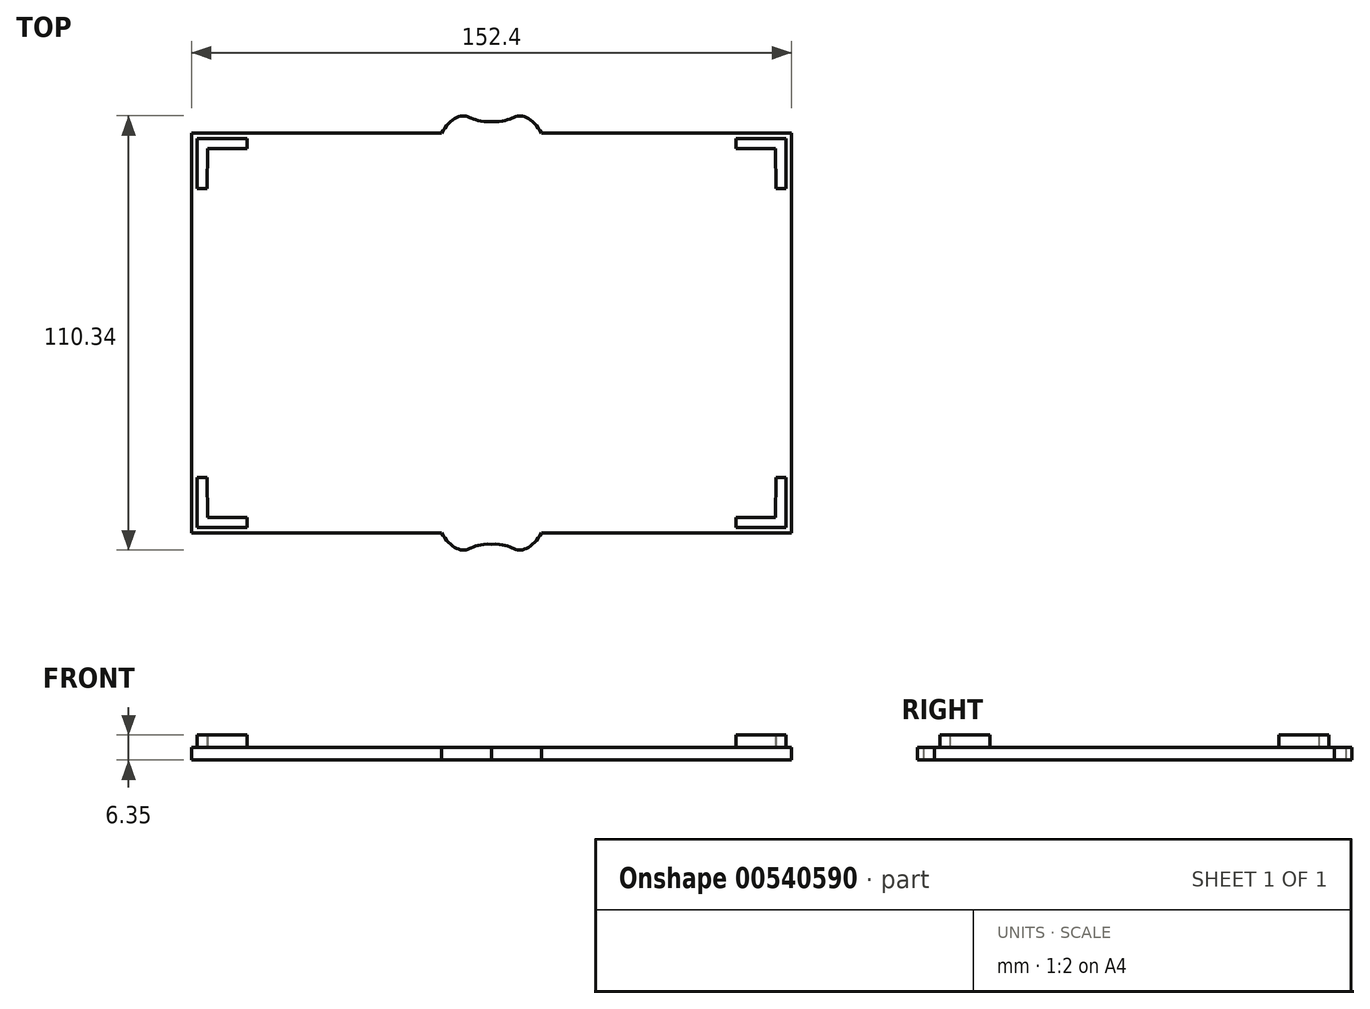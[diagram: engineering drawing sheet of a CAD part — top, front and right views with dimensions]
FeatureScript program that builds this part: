
annotation { "Feature Type Name" : "Feature", "Feature Type Description" : "" }
export const myFeature = defineFeature(function(context is Context, id is Id, definition is map)
    precondition{}
    {
        {
            var Q0;
            Q0=qCreatedBy(makeId("Top.planeOp"),FACE);
            var sketch = newSketch(context, id + "F0", { "sketchPlane" : qUnion([Q0])});
            skLineSegment(sketch, "E0.bottom", {"start": v(-76.2, 50.9) * mm, "end": v(76.2, 50.9) * mm});
            skLineSegment(sketch, "E0.top", {"start": v(-76.2, -50.7) * mm, "end": v(76.2, -50.7) * mm});
            skLineSegment(sketch, "E0.left", {"start": v(-76.2, 50.9) * mm, "end": v(-76.2, -50.7) * mm});
            skLineSegment(sketch, "E0.right", {"start": v(76.2, 50.9) * mm, "end": v(76.2, -50.7) * mm});
            skPoint(sketch, "E1", {"position": v(0.17, 0.1) * mm});
            skLineSegment(sketch, "E2.bottom", {"start": v(-74.8, 49.5) * mm, "end": v(-62.1, 49.5) * mm});
            skLineSegment(sketch, "E2.left", {"start": v(-74.8, 49.5) * mm, "end": v(-74.8, 36.8) * mm});
            skLineSegment(sketch, "E3", {"start": v(-38.1, 62.37) * mm, "end": v(-38.1, -57.09) * mm, "construction": true});
            skLineSegment(sketch, "E4", {"start": v(0, 53.8) * mm, "end": v(0, -66.57) * mm, "construction": true});
            skLineSegment(sketch, "E5", {"start": v(38.1, 55.38) * mm, "end": v(38.1, -59.8) * mm, "construction": true});
            skLineSegment(sketch, "E6", {"start": v(85.14, 0.1) * mm, "end": v(-105.52, 0.1) * mm, "construction": true});
            skPoint(sketch, "E7", {"position": v(-72.1, 46.95) * mm});
            skLineSegment(sketch, "E8", {"start": v(-62.1, 49.5) * mm, "end": v(-62.1, 46.95) * mm});
            skLineSegment(sketch, "E9", {"start": v(-72.26, 36.8) * mm, "end": v(-74.8, 36.8) * mm});
            skLineSegment(sketch, "E10", {"start": v(-72.26, 36.8) * mm, "end": v(-72.1, 46.95) * mm});
            skLineSegment(sketch, "E11", {"start": v(-72.1, 46.95) * mm, "end": v(-62.1, 46.95) * mm});
            skLineSegment(sketch, "E12.MirrorCS", {"start": v(72.1, 46.95) * mm, "end": v(62.1, 46.95) * mm});
            skLineSegment(sketch, "E13.MirrorCS", {"start": v(62.1, 49.5) * mm, "end": v(62.1, 46.95) * mm});
            skLineSegment(sketch, "E14.MirrorCS", {"start": v(74.8, 49.5) * mm, "end": v(62.1, 49.5) * mm});
            skLineSegment(sketch, "E15.MirrorCS", {"start": v(74.8, 49.5) * mm, "end": v(74.8, 36.8) * mm});
            skLineSegment(sketch, "E16.MirrorCS", {"start": v(72.26, 36.8) * mm, "end": v(72.1, 46.95) * mm});
            skLineSegment(sketch, "E17.MirrorCS", {"start": v(72.26, 36.8) * mm, "end": v(74.8, 36.8) * mm});
            skLineSegment(sketch, "E18.MirrorCS", {"start": v(-74.8, -49.31) * mm, "end": v(-62.1, -49.31) * mm});
            skLineSegment(sketch, "E19.MirrorCS", {"start": v(-62.1, -49.31) * mm, "end": v(-62.1, -46.77) * mm});
            skLineSegment(sketch, "E20.MirrorCS", {"start": v(-72.1, -46.77) * mm, "end": v(-62.1, -46.77) * mm});
            skLineSegment(sketch, "E21.MirrorCS", {"start": v(-74.8, -49.31) * mm, "end": v(-74.8, -36.61) * mm});
            skLineSegment(sketch, "E22.MirrorCS", {"start": v(-72.26, -36.61) * mm, "end": v(-72.1, -46.77) * mm});
            skLineSegment(sketch, "E23.MirrorCS", {"start": v(-72.26, -36.61) * mm, "end": v(-74.8, -36.61) * mm});
            skLineSegment(sketch, "E24.MirrorCS", {"start": v(74.8, -49.31) * mm, "end": v(62.1, -49.31) * mm});
            skLineSegment(sketch, "E25.MirrorCS", {"start": v(62.1, -49.31) * mm, "end": v(62.1, -46.77) * mm});
            skLineSegment(sketch, "E26.MirrorCS", {"start": v(72.1, -46.77) * mm, "end": v(62.1, -46.77) * mm});
            skLineSegment(sketch, "E27.MirrorCS", {"start": v(74.8, -49.31) * mm, "end": v(74.8, -36.61) * mm});
            skLineSegment(sketch, "E28.MirrorCS", {"start": v(72.26, -36.61) * mm, "end": v(72.1, -46.77) * mm});
            skLineSegment(sketch, "E29.MirrorCS", {"start": v(72.26, -36.61) * mm, "end": v(74.8, -36.61) * mm});
            skLineSegment(sketch, "E30", {"start": v(-12.7, 55.26) * mm, "end": v(-12.7, 40.9) * mm, "construction": true});
            skLineSegment(sketch, "E31", {"start": v(12.7, 54.7) * mm, "end": v(12.7, 43.66) * mm, "construction": true});
            skPoint(sketch, "E32", {"position": v(-12.7, 50.9) * mm});
            skFitSpline(sketch, "E33", {"points": [v(-12.7, 50.9) * mm, v(-7.3, 55.26) * mm, v(0, 53.8) * mm], "startDerivative": vector(9.09, 15.87) * mm, "endDerivative": vector(24.9, 1.73) * mm});
            skFitSpline(sketch, "E34.MirrorCS", {"points": [v(12.7, 50.9) * mm, v(7.3, 55.26) * mm, v(0, 53.8) * mm], "startDerivative": vector(-9.09, 15.87) * mm, "endDerivative": vector(-24.9, 1.73) * mm});
            skFitSpline(sketch, "E35.MirrorCS", {"points": [v(-12.7, -50.7) * mm, v(-7.3, -55.08) * mm, v(0, -53.61) * mm], "startDerivative": vector(9.09, -15.87) * mm, "endDerivative": vector(24.9, -1.73) * mm});
            skFitSpline(sketch, "E36.MirrorCS", {"points": [v(12.7, -50.7) * mm, v(7.3, -55.08) * mm, v(0, -53.61) * mm], "startDerivative": vector(-9.09, -15.87) * mm, "endDerivative": vector(-24.9, -1.73) * mm});
            skSolve(sketch);
        }
        {
            var Q0;
            {var subQ0=sQuery(id+"F0.wireOp",EDGE,"E0.left");Q0=makeQuery(id+"F0.imprint","IMPRINT",FACE,{"disambiguationData":[TD([[makeQuery(id+"F0.imprint","IMPRINT",EDGE,{"derivedFrom":subQ0}),1.0]])]});}
            var Q1;
            {var subQ0=sQuery(id+"F0.wireOp",EDGE,"E35.MirrorCS");Q1=makeQuery(id+"F0.imprint","IMPRINT",FACE,{"disambiguationData":[TD([[makeQuery(id+"F0.imprint","IMPRINT",EDGE,{"derivedFrom":subQ0}),1.0]])]});}
            var Q2;
            {var subQ0=sQuery(id+"F0.wireOp",EDGE,"E33");Q2=makeQuery(id+"F0.imprint","IMPRINT",FACE,{"disambiguationData":[TD([[makeQuery(id+"F0.imprint","IMPRINT",EDGE,{"derivedFrom":subQ0}),-1.0]])]});}
            extrude(context, id + "F1", {"entities" : qUnion([Q0, Q1, Q2]), "depth" : 3.17 * mm, "offsetDistance" : 25.4 * mm});
        }
        {
            var Q0;
            Q0=makeQuery(id+"F0.imprint","IMPRINT",FACE,{"disambiguationData":[TD([[makeQuery(id+"F0.imprint","IMPRINT",EDGE,{"derivedFrom":sQuery(id+"F0.wireOp",EDGE,"E18.MirrorCS")}),1.0]])]});
            var Q1;
            Q1=makeQuery(id+"F0.imprint","IMPRINT",FACE,{"disambiguationData":[TD([[makeQuery(id+"F0.imprint","IMPRINT",EDGE,{"derivedFrom":sQuery(id+"F0.wireOp",EDGE,"E2.bottom")}),-1.0]])]});
            var Q2;
            Q2=makeQuery(id+"F0.imprint","IMPRINT",FACE,{"disambiguationData":[TD([[makeQuery(id+"F0.imprint","IMPRINT",EDGE,{"derivedFrom":sQuery(id+"F0.wireOp",EDGE,"E24.MirrorCS")}),-1.0]])]});
            var Q3;
            Q3=makeQuery(id+"F0.imprint","IMPRINT",FACE,{"disambiguationData":[TD([[makeQuery(id+"F0.imprint","IMPRINT",EDGE,{"derivedFrom":sQuery(id+"F0.wireOp",EDGE,"E12.MirrorCS")}),-1.0]])]});
            extrude(context, id + "F2", {"entities" : qUnion([Q0, Q1, Q2, Q3]), "operationType" : NewBodyOperationType.ADD, "depth" : 6.35 * mm, "offsetDistance" : 25.4 * mm});
        }
    });
